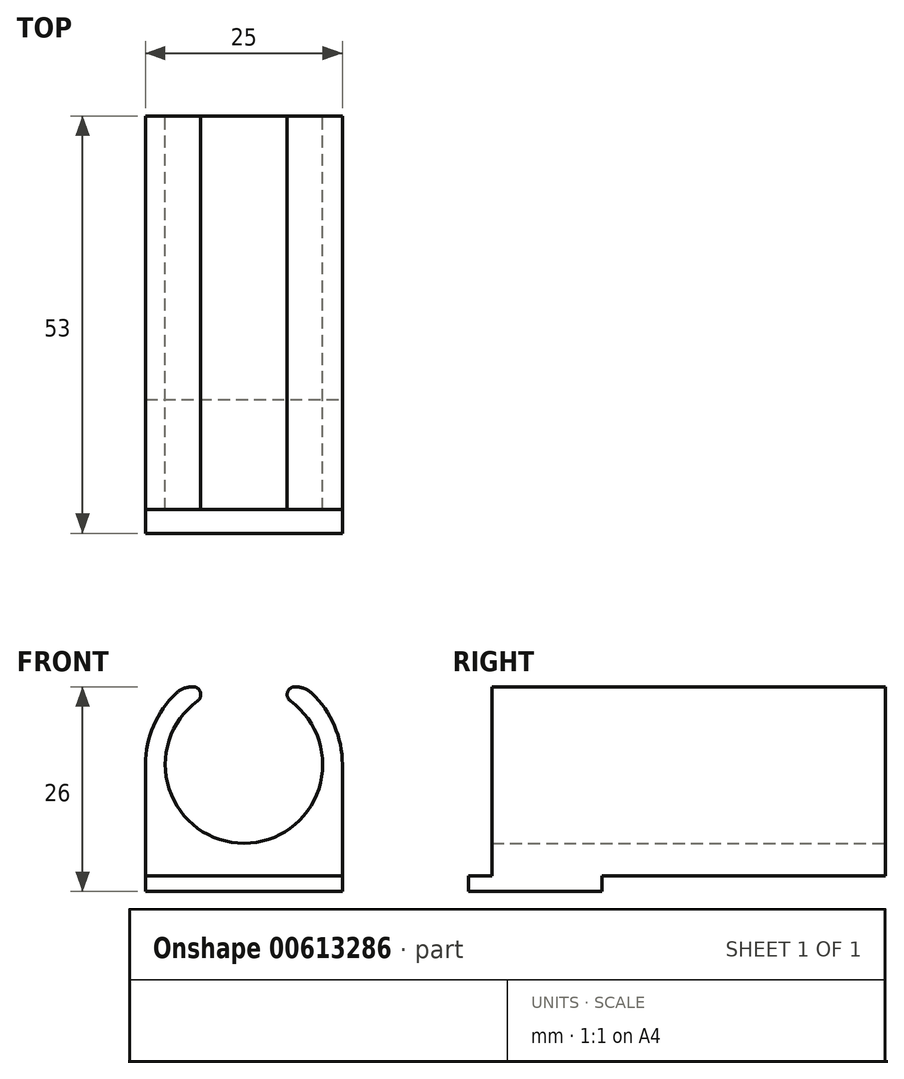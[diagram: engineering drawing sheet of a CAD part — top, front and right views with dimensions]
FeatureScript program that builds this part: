
annotation { "Feature Type Name" : "Feature", "Feature Type Description" : "" }
export const myFeature = defineFeature(function(context is Context, id is Id, definition is map)
    precondition{}
    {
        {
            var Q0;
            Q0=qCreatedBy(makeId("Front.planeOp"),FACE);
            var sketch = newSketch(context, id + "F0", { "sketchPlane" : qUnion([Q0])});
            skLineSegment(sketch, "E0.bottom", {"start": v(0, 0) * mm, "end": v(25, 0) * mm});
            skLineSegment(sketch, "E0.top", {"start": v(5.95, 24) * mm, "end": v(6.01, 24) * mm});
            skLineSegment(sketch, "E0.left", {"start": v(0, 0) * mm, "end": v(0, 14.12) * mm});
            skLineSegment(sketch, "E0.right", {"start": v(25, 0) * mm, "end": v(25, 14.12) * mm});
            skArc(sketch, "E1", {"start": v(6.6, 22.2) * mm, "mid": v(12.5, 4.12) * mm, "end": v(18.4, 22.2) * mm});
            skPoint(sketch, "E1.centerSnap0", {"position": v(12.5, 24) * mm});
            skArc(sketch, "E2", {"start": v(3.88, 23.17) * mm, "mid": v(1.01, 19.04) * mm, "end": v(0, 14.12) * mm});
            skArc(sketch, "E3.trimOffspring", {"start": v(25, 14.12) * mm, "mid": v(23.99, 19.04) * mm, "end": v(21.12, 23.17) * mm});
            skPoint(sketch, "E4.orphan", {"position": v(0, 24) * mm});
            skLineSegment(sketch, "E5.trimOffspring", {"start": v(18.99, 24) * mm, "end": v(19.05, 24) * mm});
            skPoint(sketch, "E6.orphan", {"position": v(25, 24) * mm});
            skPoint(sketch, "E7.visualSharp", {"position": v(10.97, 24) * mm});
            skArc(sketch, "E7.filletArc", {"start": v(6.6, 22.2) * mm, "mid": v(6.96, 23.31) * mm, "end": v(6.01, 24) * mm});
            skPoint(sketch, "E8.visualSharp", {"position": v(14.03, 24) * mm});
            skArc(sketch, "E8.filletArc", {"start": v(18.99, 24) * mm, "mid": v(18.04, 23.31) * mm, "end": v(18.4, 22.2) * mm});
            skPoint(sketch, "E9.visualSharp", {"position": v(4.85, 24) * mm});
            skArc(sketch, "E9.filletArc", {"start": v(5.95, 24) * mm, "mid": v(4.84, 23.79) * mm, "end": v(3.88, 23.17) * mm});
            skPoint(sketch, "E10.visualSharp", {"position": v(20.15, 24) * mm});
            skArc(sketch, "E10.filletArc", {"start": v(21.12, 23.17) * mm, "mid": v(20.16, 23.79) * mm, "end": v(19.05, 24) * mm});
            skSolve(sketch);
        }
        {
            var Q0;
            Q0=qSketchRegion(id+"F0",true);
            extrude(context, id + "F1", {"entities" : qUnion([Q0]), "depth" : 50 * mm, "offsetDistance" : 25 * mm});
        }
        {
            var Q0;
            Q0=makeQuery(id+"F1.opExtrude","SWEPT_FACE",FACE,{"disambiguationData":[OSD([sQuery(id+"F0.wireOp",EDGE,"E0.bottom")])]});
            var sketch = newSketch(context, id + "F2", { "sketchPlane" : qUnion([Q0])});
            skLineSegment(sketch, "E11.bottom", {"start": v(0, 53) * mm, "end": v(25, 53) * mm});
            skLineSegment(sketch, "E11.top", {"start": v(0, 36) * mm, "end": v(25, 36) * mm});
            skLineSegment(sketch, "E11.left", {"start": v(0, 53) * mm, "end": v(0, 36) * mm});
            skLineSegment(sketch, "E11.right", {"start": v(25, 53) * mm, "end": v(25, 36) * mm});
            skSolve(sketch);
        }
        {
            var Q0;
            Q0=qSketchRegion(id+"F2",true);
            extrude(context, id + "F3", {"entities" : qUnion([Q0]), "operationType" : NewBodyOperationType.ADD, "depth" : 2 * mm});
        }
    });
